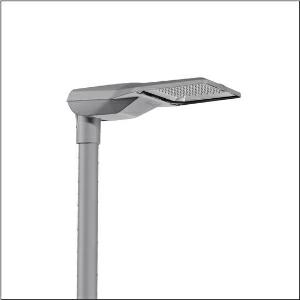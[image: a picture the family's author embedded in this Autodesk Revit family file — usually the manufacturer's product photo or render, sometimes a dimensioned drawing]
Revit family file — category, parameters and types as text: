
# Revit family: streetlight_sl_21_iq_midi___st0_5a_5xe3b31d08mb_db69
name_source: partatom
category: Lighting Fixtures
units: mm (PartAtom-declared; Revit-internal decimal feet)

## family parameters
Cut with Voids When Loaded = No
Host = Face
Light Source = No
Part Type = Normal
Room Calculation Point = No
Round Connector Dimension = Use Diameter
Shared = No

## types (1)
- --- (1 x LED, 19500 lm, 146.7 W, 3000K)
    Apparent Load = 147 VA
    CIE Flux Codes = 41 75 97 100 100
    Color Rendering = 70
    Color Temperature = 3000K
    Default Elevation = 1800 mm
    Description = Streetlight SL 21 iQ midi, mast luminaire, primary light control with lens, of PMMA, primary optical cover: cover, of toughened safety glass, transparent, light distribution: ST0.5a, light emission: direct distribution, primary light characteristic: asymmetric, installation type: post-top, side-entry, LED, High Power LED, rated luminous flux: 19.500lm, luminous efficacy: 133lm/W, light colour: 730, colour temperature: 3000K, control: Auto-Match, Temp-Guard, Lumen-Switch, Night-Set, Smart-Wire, Light-Fading, Desk-Remote (wireless, voltage-free reading and setting of iQ features in the workshop via application-optimized NFC function/RFID function), optimised constant luminous flux control (CLO 2.0), presetting dimming linear, mains connection: 230..240V, AC, 50/60Hz, start of lifetime: 147W, end of service life: 161W, reduction: 62W, luminaire housing, of diecast aluminium, powder-coated, Siteco® metallic grey (DB 702S), corrosivity category C5 mid according to DIN EN ISO 12944, please order mast flange separately, inclination adjustable: 0°, 5°, 10°, 15°, sealing non-destructively replaceable, multi-level sealing system, length: 644mm, width: 335mm, height: 110mm, mast flange for spigot size: 42mm (side-entry): 5XC10008XM4, 60/48mm (side-entry/post-top): 5XC10108XM2, 76/60mm (side-entry/post-top): 5XC10108XM1, protection rating (complete): IP66, insulation class (complete): insulation class II (safety insulation), certification: CE, ENEC, ENEC+, VDE, impact resistance: IK09, permissible operating ambient temperature for outdoor applications: -40..+50°C, standard-compliant lighting for roads and squares, packaging unit: 1 piece

Light Distribution: ST0.5a
    Height = 111 mm
    Lamp = 1 x LED
    Lamp Light Flux = 19500 lm
    Lamp Power = 146.7 W
    Lamp count = 1
    Length = 644 mm
    Luminous efficacy = 133 lm/W
    Manufacturer = Siteco
    ModVariant = No
    Model = 5XE3B31D08MB
    Number of Poles = 1
    OnlyDefault = Yes
    Power Factor = 1
    Product Name = Streetlight SL 21 iQ midi | ST0.5a
    Product group = mast luminaire | pylon top
    ProductGroupID = 6100
    Protection Class = Protection class II
    Protection Degree = IP 66
    RLX_Detail_Level = 1
    RLX_Emergency_Light_Flux = 0 lm
    RLX_Emergency_Type = 0
    RLX_Emergency_Type_DB = No
    RlxData = <blob elided: 101473 chars, md5=fb21f8e4>
    Socket = socket
    Standby Power = 0 W
    System Light Flux = 19499 lm
    System Power = 147 W
    Type Comments = factory setting: luminous flux: 100 % | dim-lin: 254 | 753 mA
    Type Image = l_1004298.jpg
    URL = http://relux.com
    VarID = @adj_144501
    Voltage = 0 V
    Weight = 0.00 kg
    Width = 336 mm

## geometry (parser evidence)
native form markers: Blend x4, Sweep x9
no freeform markers — native parametric forms only
